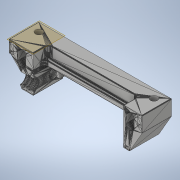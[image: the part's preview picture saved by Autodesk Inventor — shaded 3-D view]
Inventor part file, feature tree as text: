
AUTODESK INVENTOR PART (.ipt)
format: ipt  version: 2021.2 (Build 252289000, 289)  size: 8,544,256 bytes
history: mixed  units: in
note: dims shown in document units (in); Inventor stores cm internally (conversion verified against a paired STEP export)
features: hole x2, sketch x2, plane x1, imported_body x1
ambient origin geometry x8: Origin, YZ Plane, XZ Plane, XY Plane, X Axis, Y Axis, Z Axis, Center Point
bodies: Solid1 (imported_parasolid), Body1 (imported_parasolid)
feature tree (6):
  plane  "Work Plane1"
  hole  "Hole1"  [1 undecoded]
  hole  "Hole2"  [1 undecoded]
  sketch  "Sketch1"  dims[d0=0.0in d2=3.937in]
  sketch  "Sketch2"  dims[d3=3.937in d4=3.12in d5=0.2362in d6=3.316in d7=2.92in d8=90.0deg d9=0.83in d10=0.0in d11=3.937in d12=3.937in d13=3.12in d14=0.2362in d15=3.316in d16=2.92in d17=90.0deg d18=0.83in d19=0.0in]
  imported_body  NMx_Import_Brep_tag  [imported B-rep: ~16632 faces, bbox_mm=[1580.222149, 440.000019, 350.00002]]
note: 2 required parameter values undecoded (feature->parameter linkage not recoverable at this tier; creation-order binding heuristic only, values carry confidence <= 0.55)
